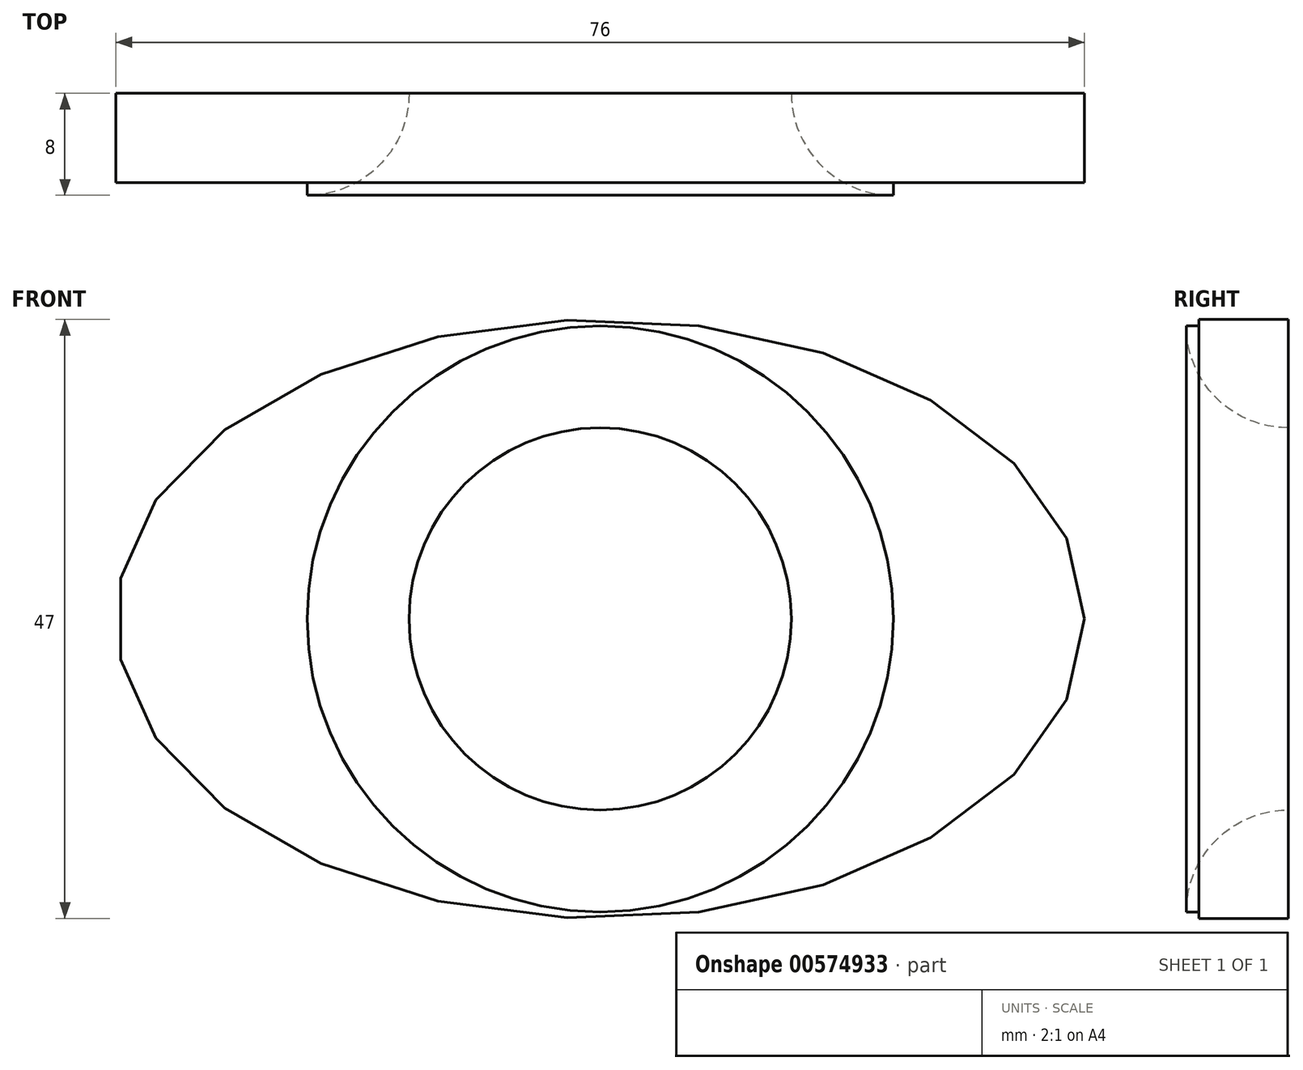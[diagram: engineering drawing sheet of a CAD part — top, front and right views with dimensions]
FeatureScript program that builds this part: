
annotation { "Feature Type Name" : "Feature", "Feature Type Description" : "" }
export const myFeature = defineFeature(function(context is Context, id is Id, definition is map)
    precondition{}
    {
        {
            var Q0;
            Q0=qCreatedBy(makeId("Front.planeOp"),FACE);
            var sketch = newSketch(context, id + "F0", { "sketchPlane" : qUnion([Q0])});
            skEllipse(sketch, "E0", {"center": v(0, 0) * mm, "majorRadius": 38 * mm, "minorRadius": 23.5 * mm, "majorAxis": v(1, 0)});
            skCircle(sketch, "E1", {"center": v(0, 0) * mm, "radius": 15 * mm});
            skSolve(sketch);
        }
        {
            var Q0;
            Q0=makeQuery(id+"F0.imprint","IMPRINT",FACE,{"disambiguationData":[TD([[makeQuery(id+"F0.imprint","IMPRINT",EDGE,{"derivedFrom":sQuery(id+"F0.wireOp",EDGE,"E0")}),1.0]])]});
            extrude(context, id + "F1", {"entities" : qUnion([Q0]), "oppositeDirection" : true, "depth" : 8 * mm, "offsetDistance" : 25 * mm});
        }
        {
            var Q0;
            Q0=makeQuery(id+"F1.opExtrude","CAP_EDGE",EDGE,{"disambiguationData":[OSD([sQuery(id+"F0.wireOp",EDGE,"E1")])],"isStart":true});
            fillet(context, id + "F2", {"entities" : qUnion([Q0]), "radius" : 8 * mm, "tangentPropagation" : true, "allowEdgeOverflow" : false});
        }
        {
            var Q0;
            Q0=makeQuery(id+"F1.opExtrude","CAP_FACE",FACE,{"disambiguationData":[OSD([sQuery(id+"F0.wireOp",EDGE,"E0"),sQuery(id+"F0.wireOp",EDGE,"E1")])],"isStart":true});
            var sketch = newSketch(context, id + "F3", { "sketchPlane" : qUnion([Q0])});
            skEllipse(sketch, "E2.0", {"center": v(0, 0) * mm, "majorRadius": 38 * mm, "minorRadius": 23.5 * mm, "majorAxis": v(1, 0)});
            skFitSpline(sketch, "E3.0", {"points": [v(37.37, -1.12) * mm, v(37.41, 0) * mm, v(37.37, 1.12) * mm, v(37.2, 2.6) * mm, v(36.75, 4.43) * mm, v(35.88, 6.58) * mm, v(34.66, 8.67) * mm, v(33.12, 10.69) * mm, v(31.26, 12.62) * mm, v(29.45, 14.13) * mm, v(27.84, 15.28) * mm, v(26.57, 16.11) * mm, v(25.22, 16.9) * mm, v(23.35, 17.9) * mm, v(20.89, 19.03) * mm, v(17.73, 20.2) * mm, v(14.42, 21.16) * mm, v(10.96, 21.93) * mm, v(7.39, 22.48) * mm, v(4.34, 22.77) * mm, v(1.87, 22.88) * mm, v(0, 22.9) * mm, v(-1.87, 22.88) * mm, v(-4.34, 22.77) * mm, v(-7.39, 22.48) * mm, v(-10.96, 21.93) * mm, v(-14.42, 21.16) * mm, v(-17.73, 20.2) * mm, v(-20.89, 19.03) * mm, v(-23.35, 17.9) * mm, v(-25.22, 16.9) * mm, v(-26.57, 16.11) * mm, v(-27.84, 15.28) * mm, v(-29.45, 14.13) * mm, v(-31.26, 12.62) * mm, v(-33.12, 10.69) * mm, v(-34.66, 8.67) * mm, v(-35.88, 6.58) * mm, v(-36.75, 4.43) * mm, v(-37.2, 2.6) * mm, v(-37.37, 1.12) * mm, v(-37.41, 0) * mm, v(-37.37, -1.12) * mm, v(-37.2, -2.6) * mm, v(-36.75, -4.43) * mm, v(-35.88, -6.58) * mm, v(-34.66, -8.67) * mm, v(-33.12, -10.69) * mm, v(-31.26, -12.62) * mm, v(-29.45, -14.13) * mm, v(-27.84, -15.28) * mm, v(-26.57, -16.11) * mm, v(-25.22, -16.9) * mm, v(-23.35, -17.9) * mm, v(-20.89, -19.03) * mm, v(-17.73, -20.2) * mm, v(-14.42, -21.16) * mm, v(-10.96, -21.93) * mm, v(-7.39, -22.48) * mm, v(-4.34, -22.77) * mm, v(-1.87, -22.88) * mm, v(0, -22.9) * mm, v(1.87, -22.88) * mm, v(4.34, -22.77) * mm, v(7.39, -22.48) * mm, v(10.96, -21.93) * mm, v(14.42, -21.16) * mm, v(17.73, -20.2) * mm, v(20.89, -19.03) * mm, v(23.35, -17.9) * mm, v(25.22, -16.9) * mm, v(26.57, -16.11) * mm, v(27.84, -15.28) * mm, v(29.45, -14.13) * mm, v(31.26, -12.62) * mm, v(33.12, -10.69) * mm, v(34.66, -8.67) * mm, v(35.88, -6.58) * mm, v(36.75, -4.43) * mm, v(37.2, -2.6) * mm, v(37.37, -1.12) * mm, v(37.41, 0) * mm, v(37.37, 1.12) * mm, v(37.37, -1.12) * mm]});
            skSolve(sketch);
        }
        {
            var Q0;
            Q0=makeQuery(id+"F3.imprint","IMPRINT",FACE,{"disambiguationData":[TD([[makeQuery(id+"F3.imprint","IMPRINT",EDGE,{"derivedFrom":sQuery(id+"F3.wireOp",EDGE,"E2.0")}),1.0]])]});
            extrude(context, id + "F4", {"entities" : qUnion([Q0]), "operationType" : NewBodyOperationType.REMOVE, "oppositeDirection" : true, "depth" : 1 * mm, "offsetDistance" : 25 * mm});
        }
    });
